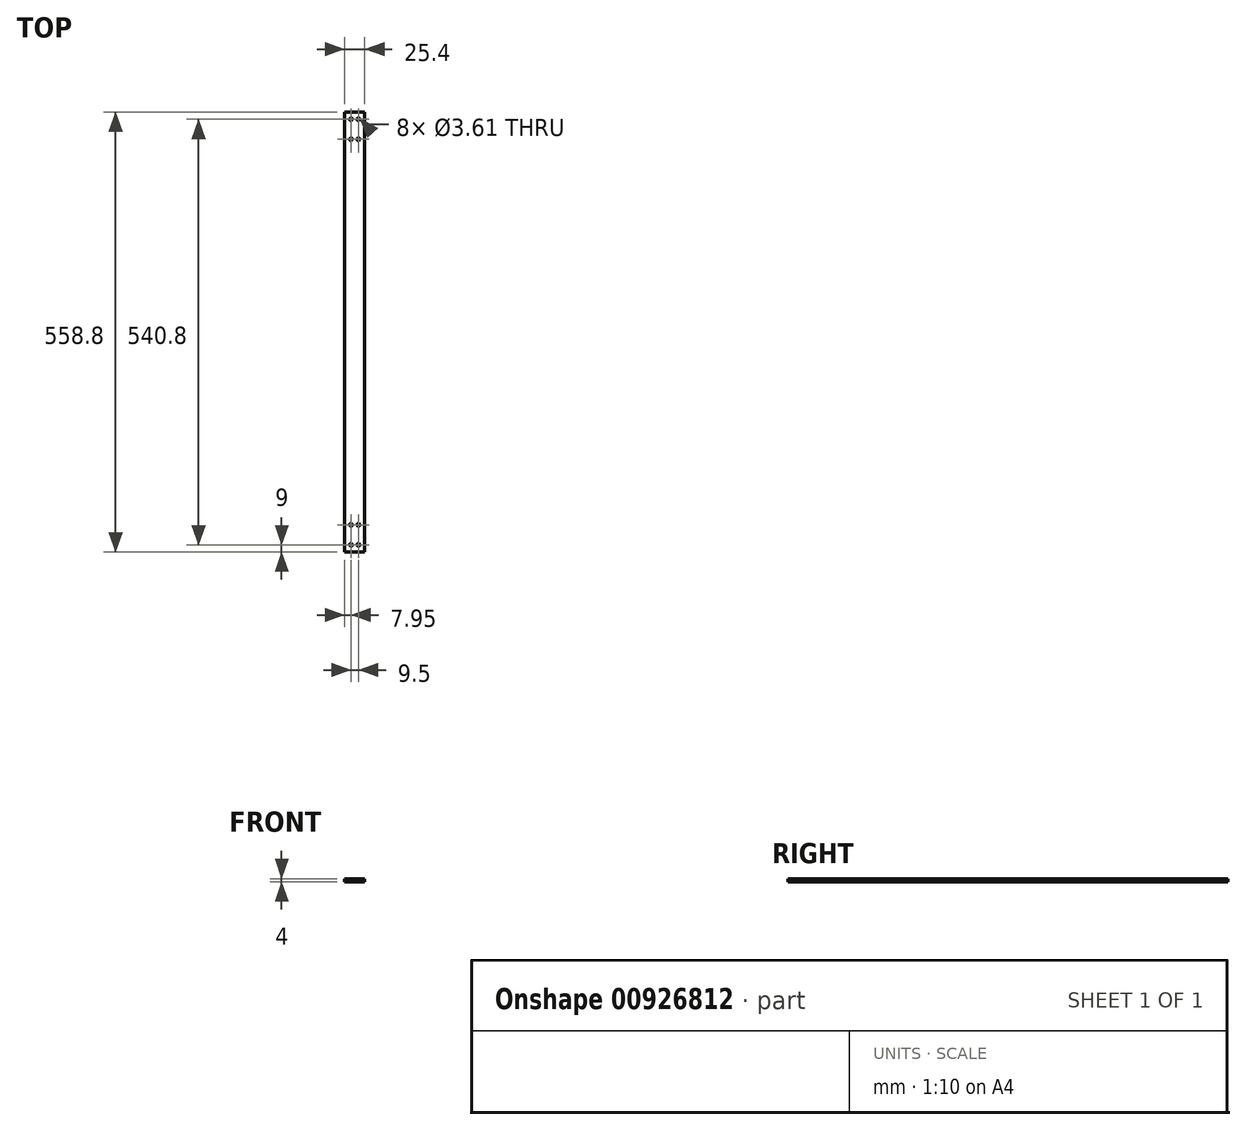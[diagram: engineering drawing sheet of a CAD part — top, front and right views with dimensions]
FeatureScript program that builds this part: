
annotation { "Feature Type Name" : "Feature", "Feature Type Description" : "" }
export const myFeature = defineFeature(function(context is Context, id is Id, definition is map)
    precondition{}
    {
        {
            var Q0;
            Q0=qCreatedBy(makeId("Front.planeOp"),FACE);
            var sketch = newSketch(context, id + "F0", { "sketchPlane" : qUnion([Q0])});
            skLineSegment(sketch, "E0.bottom", {"start": v(-12.7, 2) * mm, "end": v(12.7, 2) * mm});
            skLineSegment(sketch, "E0.top", {"start": v(-12.7, -2) * mm, "end": v(12.7, -2) * mm});
            skLineSegment(sketch, "E0.left", {"start": v(-12.7, 2) * mm, "end": v(-12.7, -2) * mm});
            skLineSegment(sketch, "E0.right", {"start": v(12.7, 2) * mm, "end": v(12.7, -2) * mm});
            skSolve(sketch);
        }
        {
            var Q0;
            Q0=makeQuery(id+"F0.imprint","IMPRINT",FACE,{"disambiguationData":[TD([[makeQuery(id+"F0.imprint","IMPRINT",EDGE,{"derivedFrom":sQuery(id+"F0.wireOp",EDGE,"E0.bottom")}),-1.0]])]});
            extrude(context, id + "F1", {"entities" : qUnion([Q0]), "endBound" : BoundingType.SYMMETRIC, "depth" : 558.8 * mm, "offsetDistance" : 25 * mm});
        }
        {
            var Q0;
            Q0=makeQuery(id+"F1.opExtrude","SWEPT_FACE",FACE,{"disambiguationData":[OSD([sQuery(id+"F0.wireOp",EDGE,"E0.bottom")])]});
            var sketch = newSketch(context, id + "F2", { "sketchPlane" : qUnion([Q0])});
            skPoint(sketch, "E1", {"position": v(-4.75, -270.4) * mm});
            skPoint(sketch, "E2", {"position": v(-4.75, -245) * mm});
            skPoint(sketch, "E3.MirrorP", {"position": v(4.75, -270.4) * mm});
            skPoint(sketch, "E4.MirrorP", {"position": v(4.75, -245) * mm});
            skPoint(sketch, "E5.MirrorP", {"position": v(4.75, 245) * mm});
            skPoint(sketch, "E6.MirrorP", {"position": v(-4.75, 245) * mm});
            skPoint(sketch, "E7.MirrorP", {"position": v(-4.75, 270.4) * mm});
            skPoint(sketch, "E8.MirrorP", {"position": v(4.75, 270.4) * mm});
            skSolve(sketch);
        }
        {
            var Q0;
            Q0=sQuery(id+"F2.wireOp",VERTEX,"E1");
            var Q1;
            Q1=sQuery(id+"F2.wireOp",VERTEX,"E2");
            var Q2;
            Q2=sQuery(id+"F2.wireOp",VERTEX,"E4.MirrorP");
            var Q3;
            Q3=sQuery(id+"F2.wireOp",VERTEX,"E3.MirrorP");
            var Q4;
            Q4=sQuery(id+"F2.wireOp",VERTEX,"E6.MirrorP");
            var Q5;
            Q5=sQuery(id+"F2.wireOp",VERTEX,"E5.MirrorP");
            var Q6;
            Q6=sQuery(id+"F2.wireOp",VERTEX,"E8.MirrorP");
            var Q7;
            Q7=sQuery(id+"F2.wireOp",VERTEX,"E7.MirrorP");
            var Q8;
            Q8=makeQuery(id+"F1.opExtrude","SWEPT_BODY",BODY,{"disambiguationData":[OSD([sQuery(id+"F0.wireOp",EDGE,"E0.bottom"),sQuery(id+"F0.wireOp",EDGE,"E0.top"),sQuery(id+"F0.wireOp",EDGE,"E0.left"),sQuery(id+"F0.wireOp",EDGE,"E0.right")])]});
            hole(context, id + "F3", {"style" : HoleStyle.SIMPLE, "endStyle" : HoleEndStyle.THROUGH, "holeDiameter" : 3.6 * mm, "majorDiameter" : 5 * mm, "isTappedThrough" : true, "tappedDepth" : 12 * mm, "tapClearance" : 3, "startFromSketch" : true, "locations" : qUnion([Q0, Q1, Q2, Q3, Q4, Q5, Q6, Q7]), "scope" : qUnion([Q8])});
        }
    });
